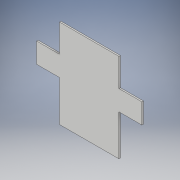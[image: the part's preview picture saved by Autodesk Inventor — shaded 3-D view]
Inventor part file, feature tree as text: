
AUTODESK INVENTOR PART (.ipt)
format: ipt  version: 2019 (Build 230136000, 136)  size: 157,184 bytes
history: native  units: in
note: dims shown in document units (in); Inventor stores cm internally (conversion verified against a paired STEP export)
features: extrude x3, sketch x3, plane x2
ambient origin geometry x8: Origin, YZ Plane, XZ Plane, XY Plane, X Axis, Y Axis, Z Axis, Center Point
bodies: Solid1 (feature_tree)
feature tree (8):
  plane  "Work Plane32"
  extrude  "Extrusion20"  Depth=3.25in
  plane  "Work Plane28"
  extrude  "Extrusion22"  Depth=1.25in
  extrude  "Extrusion24"  Depth=0.25in
  sketch  "Sketch36"  dims[d408=0.25in d409=0.0in d412=3.25in]
  sketch  "Sketch39"  dims[d413=10.0in d414=1.25in]
  sketch  "Sketch41"  dims[d415=0.2in d416=0.2in d417=0.2in d418=0.25in d419=0.0in d448=1.45in d449=0.25in d450=0.0in d284=1.0in d285=1.0in]
